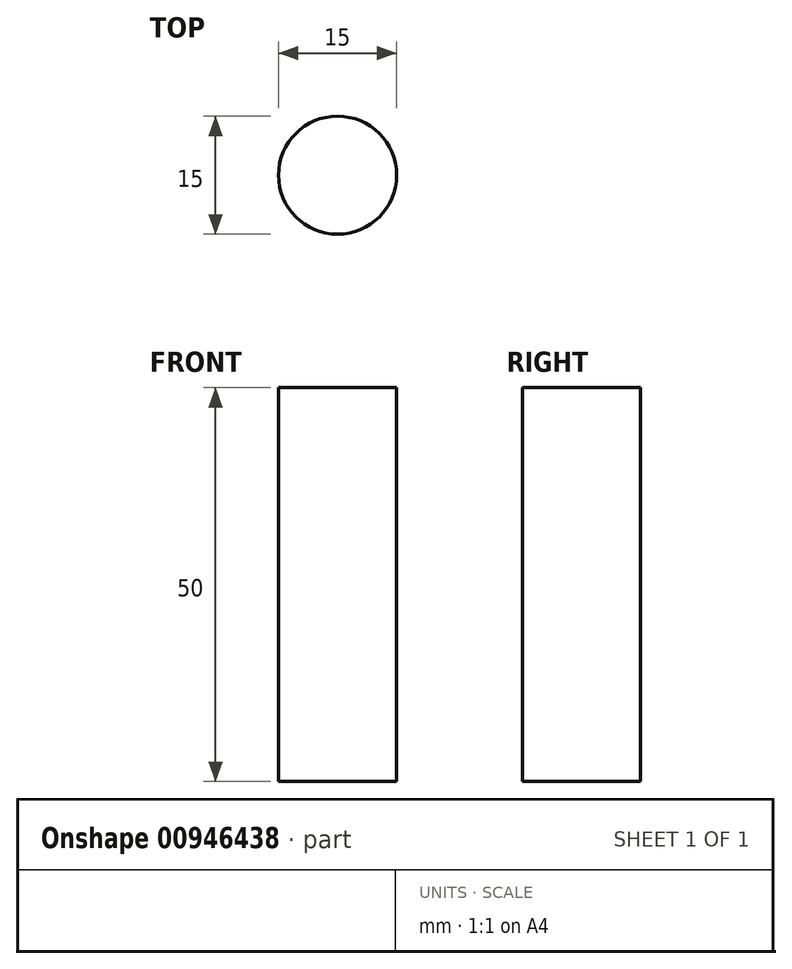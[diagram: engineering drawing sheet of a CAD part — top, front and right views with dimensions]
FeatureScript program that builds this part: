
annotation { "Feature Type Name" : "Feature", "Feature Type Description" : "" }
export const myFeature = defineFeature(function(context is Context, id is Id, definition is map)
    precondition{}
    {
        {
            var Q0;
            Q0=qCreatedBy(makeId("Top.planeOp"),FACE);
            var sketch = newSketch(context, id + "F0", { "sketchPlane" : qUnion([Q0])});
            skCircle(sketch, "E0", {"center": v(0, 0) * mm, "radius": 7.5 * mm});
            skSolve(sketch);
        }
        {
            var Q0;
            Q0 = qSketchRegion(id + "F0", true);
            extrude(context, id + "F1", {"entities" : qUnion([Q0]), "depth" : 50 * mm, "offsetDistance" : 25 * mm});
        }
    });
